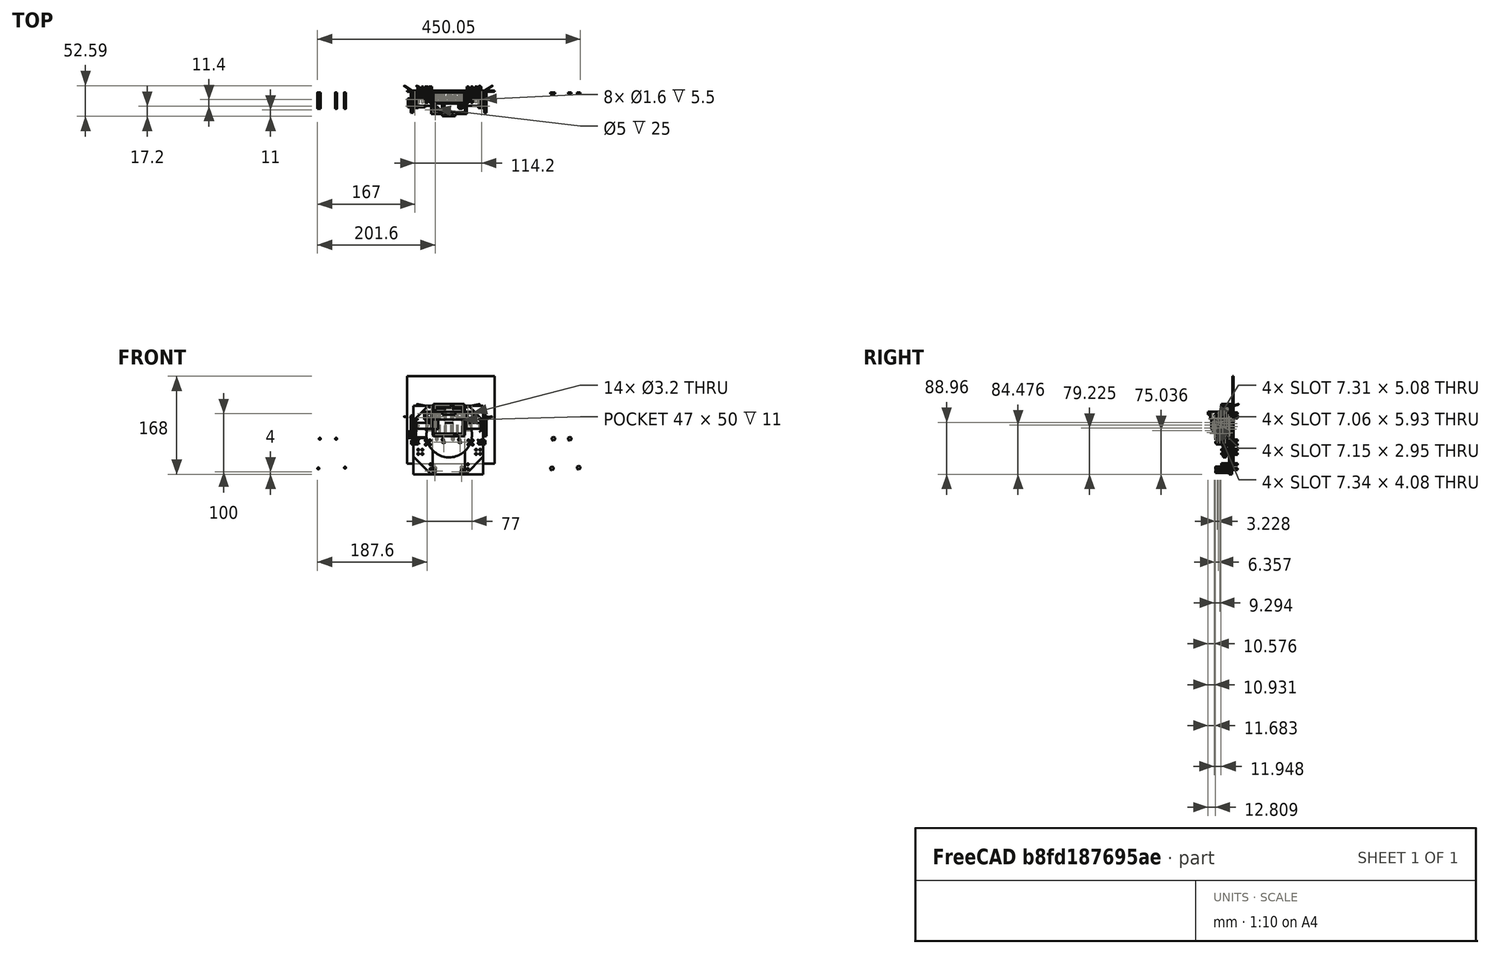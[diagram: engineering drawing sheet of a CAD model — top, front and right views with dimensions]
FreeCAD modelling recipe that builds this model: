
FCSTD DOCUMENT  (FreeCAD 0.16R6712 (Git))
Label: 5028.5 Blank Frank
License: All rights reserved
LicenseURL: http://en.wikipedia.org/wiki/All_rights_reserved
objects: Part::Cylinder×127, Part::Box×74, Part::Fuse×65, Part::Cut×64, Part::Feature×37, Part::MultiFuse×31, Part::Mirroring×14, Part::Chamfer×10, Part::Fillet×10, Part::Cone×8, Part::Compound×3, Part::Torus×2, App::DocumentObjectGroup×1
note: 445 computed .brp shape members not serialized (recipe doc carries the construction recipe); baked Part::Feature solids carry a one-line shape summary decoded from their .brp

FEATURE [Part::Cylinder] Cylinder
  Angle = 360
  Height = 30
  Radius = 7
FEATURE [Part::Cylinder] Cylinder001
  Angle = 360
  Height = 19
  Placement = pos=(0,0,30) rot=(0,0,1;0rad)
  Radius = 7
FEATURE [Part::Cylinder] Cylinder002
  Angle = 360
  Height = 1.8
  Placement = pos=(0,0,49) rot=(0,0,1;0rad)
  Radius = 2.5
FEATURE [Part::Compound] Compound
  Links = -> [Cylinder,Cylinder002,Cylinder001]
FEATURE [Part::Cylinder] Cylinder003
  Angle = 360
  Height = 30
  Radius = 7
FEATURE [Part::Cylinder] Cylinder004
  Angle = 360
  Height = 19
  Placement = pos=(0,0,30) rot=(0,0,1;0rad)
  Radius = 7
FEATURE [Part::Cylinder] Cylinder005
  Angle = 360
  Height = 1.8
  Placement = pos=(0,0,49) rot=(0,0,1;0rad)
  Radius = 2.5
FEATURE [Part::Compound] Compound001
  Links = -> [Cylinder003,Cylinder005,Cylinder004]
  Placement = pos=(14.5,0,50) rot=(1,0,0;3.14159rad)
FEATURE [Part::Cylinder] Cylinder006
  Angle = 360
  Height = 30
  Radius = 7
FEATURE [Part::Cylinder] Cylinder007
  Angle = 360
  Height = 19
  Placement = pos=(0,0,30) rot=(0,0,1;0rad)
  Radius = 7
FEATURE [Part::Cylinder] Cylinder008
  Angle = 360
  Height = 1.8
  Placement = pos=(0,0,49) rot=(0,0,1;0rad)
  Radius = 2.5
FEATURE [Part::Compound] Compound002
  Links = -> [Cylinder006,Cylinder008,Cylinder007]
  Placement = pos=(29,0,0) rot=(0,0,1;0rad)
FEATURE [Part::Box] Box  label="Cube"
  Height = 50
  Length = 47
  Placement = pos=(-9,-8,0) rot=(0,0,1;0rad)
  Width = 12
FEATURE [Part::Box] Box001  label="Cube001"
  Height = 55
  Length = 53
  Placement = pos=(-12,-8,-2.5) rot=(0,0,1;0rad)
  Width = 11
FEATURE [Part::Cylinder] Cylinder009
  Angle = 360
  Height = 50
  Radius = 7
FEATURE [Part::Cylinder] Cylinder010
  Angle = 360
  Height = 50
  Placement = pos=(14.5,0,0) rot=(0,0,1;0rad)
  Radius = 7
FEATURE [Part::Cut] Cut
  Base = -> Box001
  Tool = -> Box
FEATURE [Part::Box] Box002  label="Cube002"
  Height = 55
  Length = 53
  Placement = pos=(-12,3,-2.5) rot=(0,0,1;0rad)
  Width = 7
FEATURE [Part::Fuse] Fusion
  Base = -> Cut
  Tool = -> Box002
FEATURE [Part::Cut] Cut001  label="No idea why this is here...."
  Base = -> Fusion
  Tool = -> Cylinder009
FEATURE [Part::Cylinder] Cylinder011
  Angle = 360
  Height = 50
  Placement = pos=(29,0,0) rot=(0,0,1;0rad)
  Radius = 7
FEATURE [Part::Box] Box003  label="Cube003"
  Height = 5
  Length = 2
  Placement = pos=(28,-9,-2) rot=(0,0,1;0rad)
  Width = 12
FEATURE [Part::Box] Box004  label="Cube004"
  Height = 5
  Length = 2
  Placement = pos=(18.5,-9,46) rot=(0,0,1;0rad)
  Width = 12
FEATURE [Part::Box] Box005  label="Cube005"
  Height = 5
  Length = 2
  Placement = pos=(-2,-9,46) rot=(0,0,1;0rad)
  Width = 12
FEATURE [Part::Box] Box006  label="Cube006"
  Height = 5
  Length = 3
  Placement = pos=(35,-9,-4) rot=(0,0,1;0rad)
  Width = 12
FEATURE [Part::Cut] Cut008
FEATURE [Part::Torus] Torus001
  Angle1 = -180
  Angle2 = 180
  Angle3 = 360
  Placement = pos=(0,0,2) rot=(0,0,1;0rad)
  Radius1 = 19
  Radius2 = 1.5
FEATURE [Part::Cut] Cut009  label="wheel2"
  Base = -> Cut008
  Placement = pos=(75,-7,15) rot=(0,1,0;1.5708rad)
  Tool = -> Torus001
FEATURE [Part::Torus] Torus
  Angle1 = -180
  Angle2 = 180
  Angle3 = 360
  Placement = pos=(0,0,2) rot=(0,0,1;0rad)
  Radius1 = 19
  Radius2 = 1.5
FEATURE [Part::Cut] Cut010
FEATURE [Part::Cut] Cut011  label="wheel1"
  Base = -> Cut010
  Placement = pos=(-51,-7,15) rot=(0,1,0;1.5708rad)
  Tool = -> Torus
FEATURE [Part::Fuse] Fusion003
FEATURE [Part::Cylinder] Cylinder012
  Angle = 360
  Height = 10
  Placement = pos=(5,-4.5,0) rot=(0,1,0;1.5708rad)
  Radius = 0.8
FEATURE [Part::Fuse] Fusion048  label="right-motor001"
  Base = -> Cylinder012
  Placement = pos=(-51,-7,15) rot=(0,0,1;0rad)
  Tool = -> Fusion003
FEATURE [Part::Fuse] Fusion049
FEATURE [Part::Cylinder] Cylinder013
  Angle = 360
  Height = 10
  Placement = pos=(5,-4.5,0) rot=(0,1,0;1.5708rad)
  Radius = 0.8
FEATURE [Part::Fuse] Fusion050  label="left-motor001"
  Base = -> Cylinder013
  Placement = pos=(79,-7,15) rot=(0,0,1;3.14159rad)
  Tool = -> Fusion049
FEATURE [Part::Box] Box007  label="Cube007"
  Height = 5
  Length = 2
  Placement = pos=(37.5,-9,46) rot=(0,0,1;0rad)
  Width = 12
FEATURE [Part::Box] Box008  label="Cube008"
  Height = 5
  Length = 2
  Placement = pos=(8,-9,-2) rot=(0,0,1;0rad)
  Width = 12
FEATURE [Part::Box] Box009  label="The Ground"
  Height = 150
  Length = 150
  Placement = pos=(-57,11,-50) rot=(0,0,1;0rad)
  Width = 2
FEATURE [Part::Box] Box010  label="Motor Mount Left"
  Height = 16
  Length = 4
  Placement = pos=(69,-13,7) rot=(0,0,1;0rad)
  Width = 20
FEATURE [Part::Box] Box011  label="Motor Mount Right"
  Height = 16
  Length = 4
  Placement = pos=(-46,-13,7) rot=(0,0,1;0rad)
  Width = 20
FEATURE [Part::Box] Box012  label="Motor Support Right"
  Height = 16
  Length = 10
  Placement = pos=(-25,-1,7) rot=(0,0,1;0rad)
  Width = 8
FEATURE [Part::Box] Box013  label="Motor Support Left"
  Height = 16
  Length = 10
  Placement = pos=(43,-1,7) rot=(0,0,1;0rad)
  Width = 8
FEATURE [Part::Cylinder] Cylinder014
  Angle = 360
  Height = 28
  Placement = pos=(40.7,0,-10.3) rot=(1,0,0;1.5708rad)
  Radius = 1.6
FEATURE [Part::Cylinder] Cylinder015
  Angle = 360
  Height = 28
  Placement = pos=(-2.4,0,-59.8) rot=(1,0,0;1.5708rad)
  Radius = 1.6
FEATURE [Part::Cylinder] Cylinder016
  Angle = 360
  Height = 28
  Placement = pos=(-5,0,-9) rot=(1,0,0;1.5708rad)
  Radius = 1.6
FEATURE [Part::Cylinder] Cylinder017
  Angle = 360
  Height = 28
  Placement = pos=(25.5,0,-59.8) rot=(1,0,0;1.5708rad)
  Radius = 1.6
FEATURE [Part::Fuse] Fusion051
  Base = -> Cylinder015
  Tool = -> Cylinder016
FEATURE [Part::Fuse] Fusion052
  Base = -> Cylinder014
  Tool = -> Cylinder017
FEATURE [Part::Fuse] Fusion053  label="Screw holes on Arduino Duo"
  Base = -> Fusion051
  Tool = -> Fusion052
FEATURE [Part::Mirroring] Part__Mirroring  label="XXXXXScrew holes on Arduino Duo (Mirror #1)"
  Base = (0,0,0)
  Normal = (0,0,1)
  Placement = pos=(-204,10,-67) rot=(0,0,1;0rad)
  Source = -> Fusion053
FEATURE [Part::Box] Box014  label="Not used Cube"
  Height = 10
  Length = 10
  Placement = pos=(-1,4,-5.85) rot=(0,0,1;0rad)
  Width = 10
FEATURE [Part::Box] Box015  label="Cube014 Arduino Support cube"
  Height = 67
  Length = 55
  Placement = pos=(-13,5,-68) rot=(0,0,1;0rad)
  Width = 5
FEATURE [Part::Cylinder] Cylinder018
  Angle = 360
  Height = 5
  Placement = pos=(15,0,0) rot=(1,0,0;1.5708rad)
  Radius = 39
FEATURE [Part::Cut] Cut014  label="M3 Nut"
  Base = -> Cut001
  Placement = pos=(-6.4,10,-7.2) rot=(1,0,0;1.5708rad)
  Tool = -> Cylinder001
FEATURE [Part::Cut] Cut015  label="M3 Nut001"
  Base = -> Cut001
  Placement = pos=(21.5,10,-7.2) rot=(1,0,0;1.5708rad)
  Tool = -> Cylinder001
FEATURE [Part::Cut] Cut016  label="M3 Nut002"
  Base = -> Cut001
  Placement = pos=(36.7,10,-56.7) rot=(1,0,0;1.5708rad)
  Tool = -> Cylinder001
FEATURE [Part::Cut] Cut017  label="M3 Nut003"
  Base = -> Cut001
  Placement = pos=(-9,10,-58) rot=(1,0,0;1.5708rad)
  Tool = -> Cylinder001
FEATURE [Part::Cut] Cut018
  Base = -> Cut
  Placement = pos=(-9,10,-58) rot=(1,0,0;1.5708rad)
  Tool = -> Box006
FEATURE [Part::Cut] Cut019
  Base = -> Cut
  Placement = pos=(36.7,10,-56.7) rot=(1,0,0;1.5708rad)
  Tool = -> Box006
FEATURE [Part::Cut] Cut020
  Base = -> Cut
  Placement = pos=(-6.4,10,-7.2) rot=(1,0,0;1.5708rad)
  Tool = -> Box006
FEATURE [Part::Cut] Cut021
  Base = -> Cut
  Placement = pos=(21.5,10,-7.2) rot=(1,0,0;1.5708rad)
  Tool = -> Box006
FEATURE [Part::MultiFuse] Fusion054  label="XXXXXHex Holes"
  Placement = pos=(200,0,0) rot=(0,0,1;0rad)
  Shapes = -> [Cut018,Cut021,Cut019,Cut020]
FEATURE [Part::Box] Box016  label="Cube015"
  Height = 117
  Length = 33
  Placement = pos=(-46,7,-68) rot=(0,0,1;0rad)
  Width = 3
FEATURE [Part::Box] Box017  label="Cube016"
  Height = 117
  Length = 31
  Placement = pos=(42,7,-68) rot=(0,0,1;0rad)
  Width = 3
FEATURE [Part::Cylinder] Cylinder019
  Angle = 360
  Height = 28
  Placement = pos=(48,20,-10) rot=(1,0,0;1.5708rad)
  Radius = 1.6
FEATURE [Part::Cylinder] Cylinder020
  Angle = 360
  Height = 28
  Placement = pos=(47,20,-51) rot=(1,0,0;1.5708rad)
  Radius = 1.6
FEATURE [Part::Cylinder] Cylinder021
  Angle = 360
  Height = 28
  Placement = pos=(48,20,-17) rot=(1,0,0;1.5708rad)
  Radius = 1.6
FEATURE [Part::Cylinder] Cylinder022
  Angle = 360
  Height = 28
  Placement = pos=(47,20,-59) rot=(1,0,0;1.5708rad)
  Radius = 1.6
FEATURE [Part::Cylinder] Cylinder023
  Angle = 360
  Height = 28
  Placement = pos=(55,20,-17) rot=(1,0,0;1.5708rad)
  Radius = 1.6
FEATURE [Part::Cylinder] Cylinder024
  Angle = 360
  Height = 28
  Placement = pos=(55,20,-10) rot=(1,0,0;1.5708rad)
  Radius = 1.6
FEATURE [Part::MultiFuse] Fusion055
  Shapes = -> [Cylinder021,Cylinder023,Cylinder024,Cylinder019]
FEATURE [Part::MultiFuse] Fusion056
  Placement = pos=(13,0,-16) rot=(0,0,1;0rad)
  Shapes = -> [Cylinder021,Cylinder023,Cylinder024,Cylinder019]
FEATURE [Part::MultiFuse] Fusion057  label="Mount holes top left"
  Placement = pos=(-1,0,46) rot=(0,0,1;0rad)
  Shapes = -> [Cylinder021,Cylinder023,Cylinder024,Cylinder019]
FEATURE [Part::MultiFuse] Fusion058  label="Mount holes top right"
  Placement = pos=(-71,0,46) rot=(0,0,1;0rad)
  Shapes = -> [Cylinder021,Cylinder023,Cylinder024,Cylinder019]
FEATURE [Part::MultiFuse] Fusion059
  Shapes = -> [Cylinder022,Cylinder020,Fusion055,Fusion056]
FEATURE [Part::Mirroring] Part__Mirroring001  label="Mount holes bottom right"
  Base = (0,0,0)
  Normal = (1,0,0)
  Placement = pos=(30,0,0) rot=(0,0,1;0rad)
  Source = -> Fusion059
FEATURE [Part::Cylinder] Cylinder025
  Angle = 360
  Height = 28
  Placement = pos=(48,20,-10) rot=(1,0,0;1.5708rad)
  Radius = 1.6
FEATURE [Part::Cylinder] Cylinder026
  Angle = 360
  Height = 28
  Placement = pos=(47,20,-51) rot=(1,0,0;1.5708rad)
  Radius = 1.6
FEATURE [Part::Cylinder] Cylinder027
  Angle = 360
  Height = 28
  Placement = pos=(48,20,-17) rot=(1,0,0;1.5708rad)
  Radius = 1.6
FEATURE [Part::Cylinder] Cylinder028
  Angle = 360
  Height = 28
  Placement = pos=(47,20,-59) rot=(1,0,0;1.5708rad)
  Radius = 1.6
FEATURE [Part::Cylinder] Cylinder029
  Angle = 360
  Height = 28
  Placement = pos=(55,20,-17) rot=(1,0,0;1.5708rad)
  Radius = 1.6
FEATURE [Part::Cylinder] Cylinder030
  Angle = 360
  Height = 28
  Placement = pos=(55,20,-10) rot=(1,0,0;1.5708rad)
  Radius = 1.6
FEATURE [Part::MultiFuse] Fusion060
  Shapes = -> [Cylinder027,Cylinder029,Cylinder030,Cylinder025]
FEATURE [Part::MultiFuse] Fusion061
  Placement = pos=(13,0,-16) rot=(0,0,1;0rad)
  Shapes = -> [Cylinder027,Cylinder029,Cylinder030,Cylinder025]
FEATURE [Part::MultiFuse] Fusion062  label="Mount holes bottom left"
  Shapes = -> [Cylinder028,Cylinder026,Fusion060,Fusion061]
FEATURE [Part::Cylinder] Cylinder031  label="Cylinder127"
  Angle = 360
  Height = 10
  Placement = pos=(0,18,29) rot=(0,0,1;0rad)
  Radius = 2.25
FEATURE [Part::Cylinder] Cylinder032  label="Cylinder128"
  Angle = 360
  Height = 10
  Placement = pos=(4.5,18,32) rot=(0,0,1;0rad)
  Radius = 1
FEATURE [Part::Cylinder] Cylinder033  label="Cylinder129"
  Angle = 360
  Height = 10
  Placement = pos=(-4.5,18,32) rot=(0,0,1;0rad)
  Radius = 1
FEATURE [Part::Fuse] Fusion009  label="Mounting Screw Holes"
  Base = -> Cylinder032
  Tool = -> Cylinder033
FEATURE [Part::Fuse] Fusion071  label="Motor Holes Left"
  Base = -> Cylinder031
  Placement = pos=(37,-7,-3) rot=(0.57735,0.57735,0.57735;2.0944rad)
  Tool = -> Fusion009
FEATURE [Part::Cylinder] Cylinder034  label="Cylinder130"
  Angle = 360
  Height = 10
  Placement = pos=(0,18,29) rot=(0,0,1;0rad)
  Radius = 2.25
FEATURE [Part::Cylinder] Cylinder035  label="Cylinder131"
  Angle = 360
  Height = 10
  Placement = pos=(4.5,18,32) rot=(0,0,1;0rad)
  Radius = 1
FEATURE [Part::Cylinder] Cylinder036  label="Cylinder132"
  Angle = 360
  Height = 10
  Placement = pos=(-4.5,18,32) rot=(0,0,1;0rad)
  Radius = 1
FEATURE [Part::Fuse] Fusion072  label="Mounting Screw Holes001"
  Base = -> Cylinder035
  Tool = -> Cylinder036
FEATURE [Part::Fuse] Fusion073  label="Motor Holes Right"
  Base = -> Cylinder034
  Placement = pos=(-79,-7,-3) rot=(0.57735,0.57735,0.57735;2.0944rad)
  Tool = -> Fusion072
FEATURE [Part::Cylinder] Cylinder037  label="Cylinder133"
  Angle = 360
  Height = 28
  Placement = pos=(40.7,0,-10.3) rot=(1,0,0;1.5708rad)
  Radius = 1.6
FEATURE [Part::Cylinder] Cylinder038  label="Cylinder134"
  Angle = 360
  Height = 28
  Placement = pos=(-2.4,0,-59.8) rot=(1,0,0;1.5708rad)
  Radius = 1.6
FEATURE [Part::Cylinder] Cylinder039  label="Cylinder135"
  Angle = 360
  Height = 28
  Placement = pos=(-5,0,-9) rot=(1,0,0;1.5708rad)
  Radius = 1.6
FEATURE [Part::Cylinder] Cylinder040  label="Cylinder136"
  Angle = 360
  Height = 28
  Placement = pos=(25.5,0,-59.8) rot=(1,0,0;1.5708rad)
  Radius = 1.6
FEATURE [Part::Fuse] Fusion074
  Base = -> Cylinder038
  Tool = -> Cylinder039
FEATURE [Part::Fuse] Fusion075
  Base = -> Cylinder037
  Tool = -> Cylinder040
FEATURE [Part::Fuse] Fusion076  label="Screw holes on Arduino Duo001"
  Base = -> Fusion074
  Tool = -> Fusion075
FEATURE [Part::Mirroring] Part__Mirroring002  label="Screw holes on Arduino Duo (Mirror #1)001"
  Base = (0,0,0)
  Normal = (0,0,1)
  Placement = pos=(-4,10,-67) rot=(0,0,1;0rad)
  Source = -> Fusion076
FEATURE [Part::Mirroring] Part__Mirroring003  label="Screw holes on Arduino Duo (Mirror #1)001 (Mirror #4)"
  Base = (0,0,0)
  Normal = (1,0,0)
  Placement = pos=(27,0,-6) rot=(0,0,1;0rad)
  Source = -> Part__Mirroring002
FEATURE [Part::Box] Box018  label="Cube017"
  Height = 50
  Length = 47
  Placement = pos=(-9,-8,0) rot=(0,0,1;0rad)
  Width = 12
FEATURE [Part::Box] Box019  label="Cube018"
  Height = 55
  Length = 53
  Placement = pos=(-12,-8,-2.5) rot=(0,0,1;0rad)
  Width = 11
FEATURE [Part::Cut] Cut031
  Base = -> Box019
  Tool = -> Box018
FEATURE [Part::Box] Box020  label="Cube019"
  Height = 5
  Length = 3
  Placement = pos=(35,-9,-4) rot=(0,0,1;0rad)
  Width = 12
FEATURE [Part::Cut] Cut032
  Base = -> Cut031
  Placement = pos=(-9,10,-58) rot=(1,0,0;1.5708rad)
  Tool = -> Box020
FEATURE [Part::Cut] Cut033
  Base = -> Cut031
  Placement = pos=(36.7,10,-56.7) rot=(1,0,0;1.5708rad)
  Tool = -> Box020
FEATURE [Part::Cut] Cut034
  Base = -> Cut031
  Placement = pos=(-6.4,10,-7.2) rot=(1,0,0;1.5708rad)
  Tool = -> Box020
FEATURE [Part::Cut] Cut035
  Base = -> Cut031
  Placement = pos=(21.5,10,-7.2) rot=(1,0,0;1.5708rad)
  Tool = -> Box020
FEATURE [Part::MultiFuse] Fusion077
  Shapes = -> [Cut032,Cut035,Cut033,Cut034]
FEATURE [Part::Mirroring] Part__Mirroring004  label="Hex Holes"
  Base = (0,0,0)
  Normal = (1,0,0)
  Placement = pos=(27,0,-6) rot=(0,0,1;0rad)
  Source = -> Fusion077
FEATURE [Part::Box] Box021  label="Cube020"
  Height = 13
  Length = 61
  Placement = pos=(-16,-27,26) rot=(0,0,1;0rad)
  Width = 34
FEATURE [Part::Box] Box022  label="Cube021"
  Height = 13
  Length = 12
  Placement = pos=(45,4,26) rot=(0,0,1;0rad)
  Width = 3
FEATURE [Part::Box] Box023  label="Cube022"
  Height = 13
  Length = 12
  Placement = pos=(-28,4,26) rot=(0,0,1;0rad)
  Width = 3
FEATURE [Part::Box] Box024  label="Cube023"
  Height = 13
  Length = 55
  Placement = pos=(-13,-24,26) rot=(0,0,1;0rad)
  Width = 31
FEATURE [Part::Cylinder] Cylinder041  label="Cylinder137"
  Angle = 360
  Height = 28
  Placement = pos=(54,20,29) rot=(1,0,0;1.5708rad)
  Radius = 1.6
FEATURE [Part::Cylinder] Cylinder042  label="Cylinder138"
  Angle = 360
  Height = 28
  Placement = pos=(54,20,36) rot=(1,0,0;1.5708rad)
  Radius = 1.6
FEATURE [Part::Cylinder] Cylinder043  label="Cylinder139"
  Angle = 360
  Height = 28
  Placement = pos=(-23,20,29) rot=(1,0,0;1.5708rad)
  Radius = 1.6
FEATURE [Part::Cylinder] Cylinder044  label="Cylinder140"
  Angle = 360
  Height = 28
  Placement = pos=(-23,20,36) rot=(1,0,0;1.5708rad)
  Radius = 1.6
FEATURE [Part::Cylinder] Cylinder045  label="Cylinder141"
  Angle = 360
  Height = 10
  Placement = pos=(36,-17.25,32.5) rot=(0,1,0;1.5708rad)
  Radius = 2.5
FEATURE [Part::Cut] Cut037
  Base = -> Box021
  Tool = -> Box024
FEATURE [Part::Cut] Cut038
  Base = -> Cut037
  Tool = -> Cylinder045
FEATURE [Part::Box] Box025  label="Cube024"
  Height = 5
  Length = 22
  Placement = pos=(3.5,-31,34) rot=(0,0,1;0rad)
  Width = 4
FEATURE [Part::Cylinder] Cylinder046  label="Cylinder142"
  Angle = 360
  Height = 10
  Placement = pos=(20.75,-29,30) rot=(0,0,1;0rad)
  Radius = 0.85
FEATURE [Part::Cylinder] Cylinder047  label="Cylinder143"
  Angle = 360
  Height = 10
  Placement = pos=(8.25,-29,40) rot=(1,0,0;3.14159rad)
  Radius = 0.85
FEATURE [Part::Fuse] Fusion078
  Base = -> Cylinder046
  Tool = -> Cylinder047
FEATURE [Part::Cut] Cut039
  Base = -> Box025
  Tool = -> Fusion078
FEATURE [Part::Fuse] Fusion079
  Base = -> Cut038
  Tool = -> Cut039
FEATURE [Part::Fuse] Fusion080
  Base = -> Cylinder043
  Tool = -> Cylinder044
FEATURE [Part::Fuse] Fusion081
  Base = -> Cylinder041
  Tool = -> Cylinder042
FEATURE [Part::Fuse] Fusion082
  Base = -> Box023
  Tool = -> Fusion079
FEATURE [Part::Fuse] Fusion083
  Base = -> Box022
  Tool = -> Fusion082
FEATURE [Part::Cut] Cut040
  Base = -> Fusion083
  Tool = -> Fusion081
FEATURE [Part::Cut] Cut041  label="Switch Bracket"
  Base = -> Cut040
  Tool = -> Fusion080
FEATURE [Part::Cylinder] Cylinder048  label="Cylinder144"
  Angle = 360
  Height = 28
  Placement = pos=(-23,20,29) rot=(1,0,0;1.5708rad)
  Radius = 1.6
FEATURE [Part::Cylinder] Cylinder049  label="Cylinder145"
  Angle = 360
  Height = 28
  Placement = pos=(-23,20,36) rot=(1,0,0;1.5708rad)
  Radius = 1.6
FEATURE [Part::Fuse] Fusion084
  Base = -> Cylinder048
  Placement = pos=(1,0,0) rot=(0,0,1;0rad)
  Tool = -> Cylinder049
FEATURE [Part::Cylinder] Cylinder050  label="Cylinder146"
  Angle = 360
  Height = 28
  Placement = pos=(-23,20,29) rot=(1,0,0;1.5708rad)
  Radius = 1.6
FEATURE [Part::Cylinder] Cylinder051  label="Cylinder147"
  Angle = 360
  Height = 28
  Placement = pos=(-23,20,36) rot=(1,0,0;1.5708rad)
  Radius = 1.6
FEATURE [Part::Fuse] Fusion085
  Base = -> Cylinder050
  Placement = pos=(-1,0,0) rot=(0,0,1;0rad)
  Tool = -> Cylinder051
FEATURE [Part::Cut] Cut042
  Base = -> Cut041
  Tool = -> Fusion084
FEATURE [Part::Cut] Cut043  label="Switch Bracket001"
  Base = -> Cut042
  Tool = -> Fusion085
FEATURE [Part::Cylinder] Cylinder052  label="Cylinder148"
  Angle = 360
  Height = 42
  Radius = 4.8
FEATURE [Part::Cylinder] Cylinder053  label="Cylinder149"
  Angle = 360
  Height = 1.6
  Placement = pos=(0,0,42) rot=(0,0,1;0rad)
  Radius = 1.65
FEATURE [Part::Fuse] Fusion086
  Base = -> Cylinder052
  Placement = pos=(2,0,0) rot=(0,0,1;0rad)
  Tool = -> Cylinder053
FEATURE [Part::Cylinder] Cylinder054  label="Cylinder150"
  Angle = 360
  Height = 42
  Radius = 4.8
FEATURE [Part::Cylinder] Cylinder055  label="Cylinder151"
  Angle = 360
  Height = 1.6
  Placement = pos=(0,0,42) rot=(0,0,1;0rad)
  Radius = 1.65
FEATURE [Part::Fuse] Fusion087
  Base = -> Cylinder054
  Placement = pos=(12,0,0) rot=(0,0,1;0rad)
  Tool = -> Cylinder055
FEATURE [Part::Cylinder] Cylinder056  label="Cylinder152"
  Angle = 360
  Height = 42
  Radius = 4.8
FEATURE [Part::Cylinder] Cylinder057  label="Cylinder153"
  Angle = 360
  Height = 1.6
  Placement = pos=(0,0,42) rot=(0,0,1;0rad)
  Radius = 1.65
FEATURE [Part::Fuse] Fusion088
  Base = -> Cylinder056
  Placement = pos=(22,0,0) rot=(0,0,1;0rad)
  Tool = -> Cylinder057
FEATURE [Part::Cylinder] Cylinder058  label="Cylinder154"
  Angle = 360
  Height = 42
  Radius = 4.8
FEATURE [Part::Cylinder] Cylinder059  label="Cylinder155"
  Angle = 360
  Height = 1.6
  Placement = pos=(0,0,42) rot=(0,0,1;0rad)
  Radius = 1.65
FEATURE [Part::Fuse] Fusion089
  Base = -> Cylinder058
  Placement = pos=(32,0,0) rot=(0,0,1;0rad)
  Tool = -> Cylinder059
FEATURE [Part::Cylinder] Cylinder060  label="Cylinder156"
  Angle = 360
  Height = 42
  Radius = 4.8
FEATURE [Part::Cylinder] Cylinder061  label="Cylinder157"
  Angle = 360
  Height = 1.6
  Placement = pos=(0,0,42) rot=(0,0,1;0rad)
  Radius = 1.65
FEATURE [Part::Fuse] Fusion093
  Base = -> Cylinder060
  Placement = pos=(-8,0,0) rot=(0,0,1;0rad)
  Tool = -> Cylinder061
FEATURE [Part::MultiFuse] Fusion094  label="AAA Batts"
  Placement = pos=(2.5,0,2) rot=(0,0,1;0rad)
  Shapes = -> [Fusion093,Fusion086,Fusion087,Fusion088,Fusion089]
FEATURE [Part::Cylinder] Cylinder062  label="Cylinder158"
  Angle = 360
  Height = 10
  Radius = 17
FEATURE [Part::Cylinder] Cylinder063  label="Cylinder159"
  Angle = 360
  Height = 16
  Placement = pos=(0,0,-4) rot=(0,0,1;0rad)
  Radius = 10
FEATURE [Part::Cut] Cut044
  Base = -> Cylinder062
  Tool = -> Cylinder063
FEATURE [Part::Box] Box026  label="Cube025"
  Height = 20
  Length = 18
  Placement = pos=(0,0,-5) rot=(0,0,1;0rad)
  Width = 20
FEATURE [Part::Box] Box027  label="Cube026"
  Height = 20
  Length = 10
  Placement = pos=(0,0,-5) rot=(0,0,1;0.174533rad)
  Width = 20
FEATURE [Part::Cut] Cut045
  Base = -> Box027
  Tool = -> Box026
FEATURE [Part::Feature] Cut045001
  Placement = pos=(0,0,0) rot=(0,0,1;0.349066rad)
  shape: bbox 10 x 22.32 x 20 mm, 7 faces (baked)
FEATURE [Part::Feature] Cut045002
  Placement = pos=(0,0,0) rot=(0,0,1;0.698132rad)
  shape: bbox 15.32 x 20.52 x 20 mm, 7 faces (baked)
FEATURE [Part::Feature] Cut045003
  Placement = pos=(0,0,0) rot=(0,0,1;1.0472rad)
  shape: bbox 18.79 x 16.24 x 20 mm, 7 faces (baked)
FEATURE [Part::Feature] Cut045004
  Placement = pos=(0,0,0) rot=(0,0,1;1.39626rad)
  shape: bbox 20 x 10 x 20 mm, 7 faces (baked)
FEATURE [Part::Feature] Cut045005
  Placement = pos=(0,0,0) rot=(0,0,1;1.74533rad)
  shape: bbox 22.21 x 9.894 x 20 mm, 7 faces (baked)
FEATURE [Part::Feature] Cut045006
  Placement = pos=(0,0,0) rot=(0,0,1;2.0944rad)
  shape: bbox 21.75 x 12.86 x 20 mm, 7 faces (baked)
FEATURE [Part::Feature] Cut045007
  Placement = pos=(0,0,0) rot=(0,0,1;2.44346rad)
  shape: bbox 18.66 x 17.32 x 20 mm, 7 faces (baked)
FEATURE [Part::Feature] Cut045008
  Placement = pos=(0,0,0) rot=(0,0,1;2.79253rad)
  shape: bbox 13.32 x 19.7 x 20 mm, 7 faces (baked)
FEATURE [Part::Feature] Cut045009
  Placement = pos=(0,0,0) rot=(0,0,1;3.14159rad)
  shape: bbox 10.1 x 21.43 x 20 mm, 7 faces (baked)
FEATURE [Part::Feature] Cut045010
  Placement = pos=(0,0,0) rot=(0,0,1;3.49066rad)
  shape: bbox 10 x 22.32 x 20 mm, 7 faces (baked)
FEATURE [Part::Feature] Cut045011
  Placement = pos=(0,0,0) rot=(0,0,1;3.83972rad)
  shape: bbox 15.32 x 20.52 x 20 mm, 7 faces (baked)
FEATURE [Part::Feature] Cut045012
  Placement = pos=(0,0,0) rot=(0,0,1;4.18879rad)
  shape: bbox 18.79 x 16.24 x 20 mm, 7 faces (baked)
FEATURE [Part::Feature] Cut045013
  Placement = pos=(0,0,0) rot=(0,0,-1;1.74533rad)
  shape: bbox 20 x 10 x 20 mm, 7 faces (baked)
FEATURE [Part::Feature] Cut045014
  Placement = pos=(0,0,0) rot=(0,0,-1;1.39626rad)
  shape: bbox 22.21 x 9.894 x 20 mm, 7 faces (baked)
FEATURE [Part::Feature] Cut045015
  Placement = pos=(0,0,0) rot=(0,0,-1;1.0472rad)
  shape: bbox 21.75 x 12.86 x 20 mm, 7 faces (baked)
FEATURE [Part::Feature] Cut045016
  Placement = pos=(0,0,0) rot=(0,0,-1;0.698132rad)
  shape: bbox 18.66 x 17.32 x 20 mm, 7 faces (baked)
FEATURE [Part::Feature] Cut045017
  Placement = pos=(0,0,0) rot=(0,0,-1;0.349066rad)
  shape: bbox 13.32 x 19.7 x 20 mm, 7 faces (baked)
FEATURE [Part::MultiFuse] Fusion095
  Shapes = -> [Cut045001,Cut045008,Cut045010,Cut045009,Cut045005,Cut045003,Cut045006,Cut045002,Cut045004,Cut045007,Cut045016,Cut045017,Cut045011,Cut045012,Cut045013,Cut045014,Cut045015,Cut045]
FEATURE [Part::Cut] Cut045018
  Base = -> Cut044
  Placement = pos=(72,-7,15) rot=(0,1,0;1.5708rad)
  Tool = -> Fusion095
FEATURE [Part::Cut] Cut045019  label="Wheel with Spokes AB"
  Base = -> Cut009
  Tool = -> Cut045018
FEATURE [Part::Box] Box028  label="Cube027"
  Height = 5
  Length = 2
  Placement = pos=(37.5,-9,-2) rot=(0,0,1;0rad)
  Width = 12
FEATURE [Part::Box] Box029  label="Cube028"
  Height = 50
  Length = 47
  Placement = pos=(-9,-8,0) rot=(0,0,1;0rad)
  Width = 12
FEATURE [Part::Box] Box030  label="Cube029"
  Height = 55
  Length = 53
  Placement = pos=(-12,-8,-2.5) rot=(0,0,1;0rad)
  Width = 11
FEATURE [Part::Cylinder] Cylinder064  label="Cylinder160"
  Angle = 360
  Height = 50
  Radius = 7
FEATURE [Part::Cut] Cut045020
  Base = -> Box030
  Tool = -> Box029
FEATURE [Part::Box] Box031  label="Cube030"
  Height = 55
  Length = 53
  Placement = pos=(-12,3,-2.5) rot=(0,0,1;0rad)
  Width = 7
FEATURE [Part::Fuse] Fusion096
  Base = -> Cut045020
  Tool = -> Box031
FEATURE [App::DocumentObjectGroup] Group  label="Older version parts"
  Group = -> [Compound,Compound001,Compound002,Cylinder064,Cylinder010,Cylinder011,Fusion096,Part__Mirroring,Fusion054,Part__Mirroring004,Cut014,Cut015,Cut016,Cut017]
FEATURE [Part::Box] Box032  label="Battery Base"
  Height = 50
  Length = 55
  Placement = pos=(-13,3,-1) rot=(0,0,1;0rad)
  Width = 7
FEATURE [Part::Box] Box033  label="Cube031"
  Height = 30
  Length = 10
  Placement = pos=(-14,-25,9) rot=(0,0,1;0rad)
  Width = 10
FEATURE [Part::Cylinder] Cylinder065  label="Cylinder161"
  Angle = 360
  Height = 43.5
  Placement = pos=(4,0,2) rot=(0,0,1;0rad)
  Radius = 4.8
FEATURE [Part::Cylinder] Cylinder066  label="Cylinder162"
  Angle = 360
  Height = 1.6
  Placement = pos=(4,0,44) rot=(0,0,1;0rad)
  Radius = 1.65
FEATURE [Part::Fuse] Fusion097
  Base = -> Cylinder065
  Tool = -> Cylinder066
FEATURE [Part::Cylinder] Cylinder067  label="Cylinder163"
  Angle = 360
  Height = 43.5
  Placement = pos=(14,0,2) rot=(0,0,1;0rad)
  Radius = 4.8
FEATURE [Part::Cylinder] Cylinder068  label="Cylinder164"
  Angle = 360
  Height = 1.6
  Placement = pos=(14,0,44) rot=(0,0,1;0rad)
  Radius = 1.65
FEATURE [Part::Fuse] Fusion098
  Base = -> Cylinder067
  Tool = -> Cylinder068
FEATURE [Part::Cylinder] Cylinder069  label="Cylinder165"
  Angle = 360
  Height = 43.5
  Placement = pos=(24,0,2) rot=(0,0,1;0rad)
  Radius = 4.8
FEATURE [Part::Cylinder] Cylinder070  label="Cylinder166"
  Angle = 360
  Height = 1.6
  Placement = pos=(24,0,44) rot=(0,0,1;0rad)
  Radius = 1.65
FEATURE [Part::Fuse] Fusion099
  Base = -> Cylinder069
  Tool = -> Cylinder070
FEATURE [Part::Cylinder] Cylinder071  label="Cylinder167"
  Angle = 360
  Height = 43.5
  Placement = pos=(34,0,2) rot=(0,0,1;0rad)
  Radius = 4.8
FEATURE [Part::Cylinder] Cylinder072  label="Cylinder168"
  Angle = 360
  Height = 1.6
  Placement = pos=(34,0,44) rot=(0,0,1;0rad)
  Radius = 1.65
FEATURE [Part::Fuse] Fusion100
  Base = -> Cylinder071
  Tool = -> Cylinder072
FEATURE [Part::Cylinder] Cylinder073  label="Cylinder169"
  Angle = 360
  Height = 43.5
  Placement = pos=(-6,0,2) rot=(0,0,1;0rad)
  Radius = 4.8
FEATURE [Part::Cylinder] Cylinder074  label="Cylinder170"
  Angle = 360
  Height = 1.6
  Placement = pos=(-6,0,44) rot=(0,0,1;0rad)
  Radius = 1.65
FEATURE [Part::Fuse] Fusion101
  Base = -> Cylinder073
  Tool = -> Cylinder074
FEATURE [Part::MultiFuse] Fusion102  label="AAA Batts001"
  Shapes = -> [Fusion101,Fusion097,Fusion098,Fusion099,Fusion100]
FEATURE [Part::Cylinder] Cylinder075  label="Cylinder171"
  Angle = 360
  Height = 10
  Placement = pos=(-9,-20,4) rot=(0,0,1;0rad)
  Radius = 2.75
FEATURE [Part::Cylinder] Cylinder076  label="Cylinder172"
  Angle = 360
  Height = 27
  Placement = pos=(-9,-20,14) rot=(0,0,1;0rad)
  Radius = 2.5
FEATURE [Part::Fuse] Fusion103  label="phototransistor hole"
  Base = -> Cylinder075
  Tool = -> Cylinder076
FEATURE [Part::Cut] Cut045021  label="Phototransistor holder"
  Base = -> Box033
  Tool = -> Fusion103
FEATURE [Part::Fuse] Fusion104  label="Switch Mount with phototransistor hole"
  Base = -> Cut043
  Tool = -> Cut045021
FEATURE [Part::Cut] Cut045022
  Base = -> Box032
  Tool = -> Fusion102
FEATURE [Part::Box] Box034  label="Cube032"
  Height = 2.5
  Length = 55
  Placement = pos=(-13,-9,-1) rot=(0,0,1;0rad)
  Width = 12
FEATURE [Part::Box] Box035  label="Cube033"
  Height = 2.5
  Length = 55
  Placement = pos=(-13,-9,46.5) rot=(0,0,1;0rad)
  Width = 12
FEATURE [Part::Box] Box036  label="Cube034"
  Height = 50
  Length = 2.5
  Placement = pos=(-13,-9,-1) rot=(0,0,1;0rad)
  Width = 12
FEATURE [Part::Box] Box037  label="Cube035"
  Height = 50
  Length = 2.5
  Placement = pos=(39.5,-9,-1) rot=(0,0,1;0rad)
  Width = 12
FEATURE [Part::MultiFuse] Fusion105
  Shapes = -> [Box034,Box036,Box037,Box035]
FEATURE [Part::Box] Box038  label="Cube036"
  Height = 5
  Length = 2
  Placement = pos=(-10.5,-9,46) rot=(0,0,1;0rad)
  Width = 12
FEATURE [Part::Box] Box039  label="Cube037"
  Height = 5
  Length = 2
  Placement = pos=(-10.5,-9,-2) rot=(0,0,1;0rad)
  Width = 12
FEATURE [Part::MultiFuse] Fusion106
  Shapes = -> [Box039,Box038,Box028,Box007]
FEATURE [Part::MultiFuse] Fusion107
  Shapes = -> [Box003,Box004,Box005,Box008]
FEATURE [Part::Cut] Cut045023
  Base = -> Fusion105
  Tool = -> Fusion106
FEATURE [Part::Cut] Cut045024
  Base = -> Cut045023
  Tool = -> Fusion107
FEATURE [Part::Box] Box040  label="Cube038"
  Height = 1.6
  Length = 30
  Placement = pos=(-56,-15.5,-6) rot=(0,0,1;0rad)
  Width = 15
FEATURE [Part::Box] Box041  label="Cube039"
  Height = 10
  Length = 14
  Placement = pos=(-56,-10.5,-4.5) rot=(0,0,1;0rad)
  Width = 6
FEATURE [Part::Box] Box042  label="Cube040"
  Height = 10
  Length = 5.3
  Placement = pos=(-51.7,-11.5,-4.5) rot=(0,0,1;0rad)
  Width = 8
FEATURE [Part::Cut] Cut045025
  Base = -> Box041
  Tool = -> Box042
FEATURE [Part::Fuse] Fusion108  label="Spoke Sensor PCB"
  Base = -> Box040
  Tool = -> Cut045025
FEATURE [Part::Cylinder] Cylinder077  label="Cylinder173"
  Angle = 360
  Height = 14.5
  Placement = pos=(-43.6,-2.4,-9) rot=(0,0,1;0rad)
  Radius = 0.8
FEATURE [Part::Cylinder] Cylinder078  label="Cylinder174"
  Angle = 360
  Height = 14.5
  Placement = pos=(-43.6,-13.8,-9) rot=(0,0,1;0rad)
  Radius = 0.8
FEATURE [Part::Fuse] Fusion109
  Base = -> Cylinder077
  Tool = -> Cylinder078
FEATURE [Part::Cut] Cut045026  label="Spoke Sensor PCB001"
  Base = -> Fusion108
  Tool = -> Fusion109
FEATURE [Part::Cylinder] Cylinder079  label="Cylinder175"
  Angle = 360
  Height = 14.5
  Placement = pos=(-43.6,-2.4,-18) rot=(0,0,1;0rad)
  Radius = 0.8
FEATURE [Part::Cylinder] Cylinder080  label="Cylinder176"
  Angle = 360
  Height = 14.5
  Placement = pos=(-43.6,-13.8,-18) rot=(0,0,1;0rad)
  Radius = 0.8
FEATURE [Part::Fuse] Fusion110  label="Batt Holder"
  Base = -> Cut045022
  Tool = -> Cut045024
FEATURE [Part::Box] Box043  label="Cube041"
  Height = 4
  Length = 12
  Placement = pos=(-50,-16.75,-17) rot=(0,0,1;0rad)
  Width = 26.75
FEATURE [Part::Chamfer] Chamfer
  Base = -> Box043
  Edges = 1 edges r=7: [Edge3]
FEATURE [Part::Cone] Cone
  Angle = 360
  Height = 1.5
  Placement = pos=(-43.6,-2.4,-13) rot=(0,0,1;0rad)
  Radius1 = 2.75
  Radius2 = 1.25
FEATURE [Part::Cone] Cone001
  Angle = 360
  Height = 1.5
  Placement = pos=(-43.6,-13.8,-13) rot=(0,0,1;0rad)
  Radius1 = 2.75
  Radius2 = 1.25
FEATURE [Part::Fuse] Fusion111
  Base = -> Cone
  Tool = -> Cone001
FEATURE [Part::Fuse] Fusion112
  Base = -> Chamfer
  Tool = -> Fusion111
FEATURE [Part::Fuse] Fusion113
  Base = -> Cylinder079
  Tool = -> Cylinder080
FEATURE [Part::Cut] Cut045027
  Base = -> Fusion112
  Tool = -> Fusion113
FEATURE [Part::Cylinder] Cylinder081  label="Cylinder177"
  Angle = 360
  Height = 14.5
  Placement = pos=(-43.6,-2.4,-18) rot=(0,0,1;0rad)
  Radius = 0.8
FEATURE [Part::Cylinder] Cylinder082  label="Cylinder178"
  Angle = 360
  Height = 14.5
  Placement = pos=(-43.6,-13.8,-18) rot=(0,0,1;0rad)
  Radius = 0.8
FEATURE [Part::Box] Box044  label="Cube042"
  Height = 4
  Length = 12
  Placement = pos=(-50,-16.75,-17) rot=(0,0,1;0rad)
  Width = 26.75
FEATURE [Part::Chamfer] Chamfer001
  Base = -> Box044
  Edges = 1 edges r=7: [Edge3]
FEATURE [Part::Cone] Cone002
  Angle = 360
  Height = 1.5
  Placement = pos=(-43.6,-2.4,-13) rot=(0,0,1;0rad)
  Radius1 = 2.75
  Radius2 = 1.25
FEATURE [Part::Cone] Cone003
  Angle = 360
  Height = 1.5
  Placement = pos=(-43.6,-13.8,-13) rot=(0,0,1;0rad)
  Radius1 = 2.75
  Radius2 = 1.25
FEATURE [Part::Fuse] Fusion114
  Base = -> Cone002
  Tool = -> Cone003
FEATURE [Part::Fuse] Fusion115
  Base = -> Chamfer001
  Tool = -> Fusion114
FEATURE [Part::Fuse] Fusion116
  Base = -> Cylinder081
  Tool = -> Cylinder082
FEATURE [Part::Cut] Cut045028
  Base = -> Fusion115
  Tool = -> Fusion116
FEATURE [Part::Mirroring] Part__Mirroring005  label="Cut045028 (Mirror #6)"
  Base = (0,0,0)
  Normal = (1,0,0)
  Placement = pos=(27,0,0) rot=(0,0,1;0rad)
  Source = -> Cut045028
FEATURE [Part::Box] Box045  label="Cube043"
  Height = 5
  Length = 2
  Placement = pos=(28,-9,-2) rot=(0,0,1;0rad)
  Width = 12
FEATURE [Part::Box] Box046  label="Cube044"
  Height = 5
  Length = 2
  Placement = pos=(18.5,-9,46) rot=(0,0,1;0rad)
  Width = 12
FEATURE [Part::Box] Box047  label="Cube045"
  Height = 5
  Length = 2
  Placement = pos=(-2,-9,46) rot=(0,0,1;0rad)
  Width = 12
FEATURE [Part::Box] Box048  label="Cube046"
  Height = 5
  Length = 2
  Placement = pos=(37.5,-9,46) rot=(0,0,1;0rad)
  Width = 12
FEATURE [Part::Box] Box049  label="Cube047"
  Height = 5
  Length = 2
  Placement = pos=(8,-9,-2) rot=(0,0,1;0rad)
  Width = 12
FEATURE [Part::Box] Box050  label="Motor Mount Left001"
  Height = 16
  Length = 4
  Placement = pos=(69,-13,7) rot=(0,0,1;0rad)
  Width = 20
FEATURE [Part::Box] Box051  label="Motor Mount Right001"
  Height = 16
  Length = 4
  Placement = pos=(-46,-13,7) rot=(0,0,1;0rad)
  Width = 20
FEATURE [Part::Box] Box052  label="Motor Support Right001"
  Height = 16
  Length = 10
  Placement = pos=(-25,-1,7) rot=(0,0,1;0rad)
  Width = 8
FEATURE [Part::Box] Box053  label="Motor Support Left001"
  Height = 16
  Length = 10
  Placement = pos=(43,-1,7) rot=(0,0,1;0rad)
  Width = 8
FEATURE [Part::Box] Box054  label="Cube014 Arduino Support cube001"
  Height = 67
  Length = 55
  Placement = pos=(-13,5,-68) rot=(0,0,1;0rad)
  Width = 5
FEATURE [Part::Box] Box055  label="Cube048"
  Height = 117
  Length = 33
  Placement = pos=(-46,7,-68) rot=(0,0,1;0rad)
  Width = 3
FEATURE [Part::Box] Box056  label="Cube049"
  Height = 117
  Length = 31
  Placement = pos=(42,7,-68) rot=(0,0,1;0rad)
  Width = 3
FEATURE [Part::Cylinder] Cylinder083  label="Cylinder179"
  Angle = 360
  Height = 28
  Placement = pos=(48,20,-10) rot=(1,0,0;1.5708rad)
  Radius = 1.6
FEATURE [Part::Cylinder] Cylinder084  label="Cylinder180"
  Angle = 360
  Height = 28
  Placement = pos=(48,20,-17) rot=(1,0,0;1.5708rad)
  Radius = 1.6
FEATURE [Part::Cylinder] Cylinder085  label="Cylinder181"
  Angle = 360
  Height = 28
  Placement = pos=(55,20,-17) rot=(1,0,0;1.5708rad)
  Radius = 1.6
FEATURE [Part::Cylinder] Cylinder086  label="Cylinder182"
  Angle = 360
  Height = 28
  Placement = pos=(55,20,-10) rot=(1,0,0;1.5708rad)
  Radius = 1.6
FEATURE [Part::MultiFuse] Fusion117  label="Mount holes top left001"
  Placement = pos=(-1,0,46) rot=(0,0,1;0rad)
  Shapes = -> [Cylinder084,Cylinder085,Cylinder086,Cylinder083]
FEATURE [Part::MultiFuse] Fusion118  label="Mount holes top right001"
  Placement = pos=(-71,0,46) rot=(0,0,1;0rad)
  Shapes = -> [Cylinder084,Cylinder085,Cylinder086,Cylinder083]
FEATURE [Part::Cylinder] Cylinder087  label="Cylinder183"
  Angle = 360
  Height = 10
  Placement = pos=(0,18,29) rot=(0,0,1;0rad)
  Radius = 2.25
FEATURE [Part::Cylinder] Cylinder088  label="Cylinder184"
  Angle = 360
  Height = 10
  Placement = pos=(4.5,18,32) rot=(0,0,1;0rad)
  Radius = 1
FEATURE [Part::Cylinder] Cylinder089  label="Cylinder185"
  Angle = 360
  Height = 10
  Placement = pos=(-4.5,18,32) rot=(0,0,1;0rad)
  Radius = 1
FEATURE [Part::Fuse] Fusion119  label="Mounting Screw Holes002"
  Base = -> Cylinder088
  Tool = -> Cylinder089
FEATURE [Part::Fuse] Fusion120  label="Motor Holes Left001"
  Base = -> Cylinder087
  Placement = pos=(37,-7,-3) rot=(0.57735,0.57735,0.57735;2.0944rad)
  Tool = -> Fusion119
FEATURE [Part::Cylinder] Cylinder090  label="Cylinder186"
  Angle = 360
  Height = 10
  Placement = pos=(0,18,29) rot=(0,0,1;0rad)
  Radius = 2.25
FEATURE [Part::Cylinder] Cylinder091  label="Cylinder187"
  Angle = 360
  Height = 10
  Placement = pos=(4.5,18,32) rot=(0,0,1;0rad)
  Radius = 1
FEATURE [Part::Cylinder] Cylinder092  label="Cylinder188"
  Angle = 360
  Height = 10
  Placement = pos=(-4.5,18,32) rot=(0,0,1;0rad)
  Radius = 1
FEATURE [Part::Fuse] Fusion121  label="Mounting Screw Holes003"
  Base = -> Cylinder091
  Tool = -> Cylinder092
FEATURE [Part::Fuse] Fusion122  label="Motor Holes Right001"
  Base = -> Cylinder090
  Placement = pos=(-79,-7,-3) rot=(0.57735,0.57735,0.57735;2.0944rad)
  Tool = -> Fusion121
FEATURE [Part::Cylinder] Cylinder093  label="Cylinder189"
  Angle = 360
  Height = 28
  Placement = pos=(40.7,0,-10.3) rot=(1,0,0;1.5708rad)
  Radius = 1.6
FEATURE [Part::Cylinder] Cylinder094  label="Cylinder190"
  Angle = 360
  Height = 28
  Placement = pos=(-2.4,0,-59.8) rot=(1,0,0;1.5708rad)
  Radius = 1.6
FEATURE [Part::Cylinder] Cylinder095  label="Cylinder191"
  Angle = 360
  Height = 28
  Placement = pos=(-5,0,-9) rot=(1,0,0;1.5708rad)
  Radius = 1.6
FEATURE [Part::Cylinder] Cylinder096  label="Cylinder192"
  Angle = 360
  Height = 28
  Placement = pos=(25.5,0,-59.8) rot=(1,0,0;1.5708rad)
  Radius = 1.6
FEATURE [Part::Fuse] Fusion123
  Base = -> Cylinder094
  Tool = -> Cylinder095
FEATURE [Part::Fuse] Fusion124
  Base = -> Cylinder093
  Tool = -> Cylinder096
FEATURE [Part::Fuse] Fusion125  label="Screw holes on Arduino Duo002"
  Base = -> Fusion123
  Tool = -> Fusion124
FEATURE [Part::Mirroring] Part__Mirroring006  label="Screw holes on Arduino Duo (Mirror #1)002"
  Base = (0,0,0)
  Normal = (0,0,1)
  Placement = pos=(-4,10,-67) rot=(0,0,1;0rad)
  Source = -> Fusion125
FEATURE [Part::Mirroring] Part__Mirroring007  label="Screw holes on Arduino Duo (Mirror #1)001 (Mirror #4)001"
  Base = (0,0,0)
  Normal = (1,0,0)
  Placement = pos=(27,0,-6) rot=(0,0,1;0rad)
  Source = -> Part__Mirroring006
FEATURE [Part::Box] Box057  label="Cube050"
  Height = 50
  Length = 47
  Placement = pos=(-9,-8,0) rot=(0,0,1;0rad)
  Width = 12
FEATURE [Part::Box] Box058  label="Cube051"
  Height = 55
  Length = 53
  Placement = pos=(-12,-8,-2.5) rot=(0,0,1;0rad)
  Width = 11
FEATURE [Part::Cut] Cut045029
  Base = -> Box058
  Tool = -> Box057
FEATURE [Part::Box] Box059  label="Cube052"
  Height = 5
  Length = 3
  Placement = pos=(35,-9,-4) rot=(0,0,1;0rad)
  Width = 12
FEATURE [Part::Cut] Cut045030
  Base = -> Cut045029
  Placement = pos=(-9,10,-58) rot=(1,0,0;1.5708rad)
  Tool = -> Box059
FEATURE [Part::Cut] Cut045031
  Base = -> Cut045029
  Placement = pos=(36.7,10,-56.7) rot=(1,0,0;1.5708rad)
  Tool = -> Box059
FEATURE [Part::Cut] Cut045032
  Base = -> Cut045029
  Placement = pos=(-6.4,10,-7.2) rot=(1,0,0;1.5708rad)
  Tool = -> Box059
FEATURE [Part::Cut] Cut045033
  Base = -> Cut045029
  Placement = pos=(21.5,10,-7.2) rot=(1,0,0;1.5708rad)
  Tool = -> Box059
FEATURE [Part::MultiFuse] Fusion126
  Shapes = -> [Cut045030,Cut045033,Cut045031,Cut045032]
FEATURE [Part::Mirroring] Part__Mirroring008  label="Hex Holes001"
  Base = (0,0,0)
  Normal = (1,0,0)
  Placement = pos=(27,0,-6) rot=(0,0,1;0rad)
  Source = -> Fusion126
FEATURE [Part::Box] Box060  label="Cube053"
  Height = 5
  Length = 2
  Placement = pos=(37.5,-9,-2) rot=(0,0,1;0rad)
  Width = 12
FEATURE [Part::Box] Box061  label="Battery Base001"
  Height = 50
  Length = 55
  Placement = pos=(-13,3,-1) rot=(0,0,1;0rad)
  Width = 7
FEATURE [Part::Cylinder] Cylinder097  label="Cylinder193"
  Angle = 360
  Height = 42
  Radius = 4.8
FEATURE [Part::Cylinder] Cylinder098  label="Cylinder194"
  Angle = 360
  Height = 1.6
  Placement = pos=(0,0,42) rot=(0,0,1;0rad)
  Radius = 1.65
FEATURE [Part::Fuse] Fusion127
  Base = -> Cylinder097
  Placement = pos=(2,0,0) rot=(0,0,1;0rad)
  Tool = -> Cylinder098
FEATURE [Part::Cylinder] Cylinder099  label="Cylinder195"
  Angle = 360
  Height = 42
  Radius = 4.8
FEATURE [Part::Cylinder] Cylinder100  label="Cylinder196"
  Angle = 360
  Height = 1.6
  Placement = pos=(0,0,42) rot=(0,0,1;0rad)
  Radius = 1.65
FEATURE [Part::Fuse] Fusion128
  Base = -> Cylinder099
  Placement = pos=(12,0,0) rot=(0,0,1;0rad)
  Tool = -> Cylinder100
FEATURE [Part::Cylinder] Cylinder101  label="Cylinder197"
  Angle = 360
  Height = 42
  Radius = 4.8
FEATURE [Part::Cylinder] Cylinder102  label="Cylinder198"
  Angle = 360
  Height = 1.6
  Placement = pos=(0,0,42) rot=(0,0,1;0rad)
  Radius = 1.65
FEATURE [Part::Fuse] Fusion129
  Base = -> Cylinder101
  Placement = pos=(22,0,0) rot=(0,0,1;0rad)
  Tool = -> Cylinder102
FEATURE [Part::Cylinder] Cylinder103  label="Cylinder199"
  Angle = 360
  Height = 42
  Radius = 4.8
FEATURE [Part::Cylinder] Cylinder104  label="Cylinder200"
  Angle = 360
  Height = 1.6
  Placement = pos=(0,0,42) rot=(0,0,1;0rad)
  Radius = 1.65
FEATURE [Part::Fuse] Fusion130
  Base = -> Cylinder103
  Placement = pos=(32,0,0) rot=(0,0,1;0rad)
  Tool = -> Cylinder104
FEATURE [Part::Cylinder] Cylinder105  label="Cylinder201"
  Angle = 360
  Height = 42
  Radius = 4.8
FEATURE [Part::Cylinder] Cylinder106  label="Cylinder202"
  Angle = 360
  Height = 1.6
  Placement = pos=(0,0,42) rot=(0,0,1;0rad)
  Radius = 1.65
FEATURE [Part::Fuse] Fusion131
  Base = -> Cylinder105
  Placement = pos=(-8,0,0) rot=(0,0,1;0rad)
  Tool = -> Cylinder106
FEATURE [Part::MultiFuse] Fusion132  label="AAA Batts002"
  Placement = pos=(2,0,2) rot=(0,0,1;0rad)
  Shapes = -> [Fusion131,Fusion127,Fusion128,Fusion129,Fusion130]
FEATURE [Part::Cut] Cut045034
  Base = -> Box061
  Tool = -> Fusion132
FEATURE [Part::Box] Box062  label="Cube054"
  Height = 2.5
  Length = 55
  Placement = pos=(-13,-9,-1) rot=(0,0,1;0rad)
  Width = 12
FEATURE [Part::Box] Box063  label="Cube055"
  Height = 2.5
  Length = 55
  Placement = pos=(-13,-9,46.5) rot=(0,0,1;0rad)
  Width = 12
FEATURE [Part::Box] Box064  label="Cube056"
  Height = 50
  Length = 2.5
  Placement = pos=(-13,-9,-1) rot=(0,0,1;0rad)
  Width = 12
FEATURE [Part::Box] Box065  label="Cube057"
  Height = 50
  Length = 2.5
  Placement = pos=(39.5,-9,-1) rot=(0,0,1;0rad)
  Width = 12
FEATURE [Part::MultiFuse] Fusion133
  Shapes = -> [Box062,Box064,Box065,Box063]
FEATURE [Part::Box] Box066  label="Cube058"
  Height = 5
  Length = 2
  Placement = pos=(-10.5,-9,46) rot=(0,0,1;0rad)
  Width = 12
FEATURE [Part::Box] Box067  label="Cube059"
  Height = 5
  Length = 2
  Placement = pos=(-10.5,-9,-2) rot=(0,0,1;0rad)
  Width = 12
FEATURE [Part::MultiFuse] Fusion134
  Shapes = -> [Box067,Box066,Box060,Box048]
FEATURE [Part::MultiFuse] Fusion135
  Shapes = -> [Box045,Box046,Box047,Box049]
FEATURE [Part::Cut] Cut045035
  Base = -> Fusion133
  Tool = -> Fusion134
FEATURE [Part::Cut] Cut045036
  Base = -> Cut045035
  Tool = -> Fusion135
FEATURE [Part::Cylinder] Cylinder107  label="Cylinder203"
  Angle = 360
  Height = 14.5
  Placement = pos=(-43.6,-2.4,-15) rot=(0,0,1;0rad)
  Radius = 0.8
FEATURE [Part::Cylinder] Cylinder108  label="Cylinder204"
  Angle = 360
  Height = 14.5
  Placement = pos=(-43.6,-13.8,-15) rot=(0,0,1;0rad)
  Radius = 0.8
FEATURE [Part::Fuse] Fusion136
  Base = -> Cut045034
  Tool = -> Cut045036
FEATURE [Part::Box] Box068  label="Cube060"
  Height = 4
  Length = 12
  Placement = pos=(-50,-16.75,-14) rot=(0,0,1;0rad)
  Width = 26.75
FEATURE [Part::Chamfer] Chamfer002
  Base = -> Box068
  Edges = 1 edges r=7: [Edge3]
FEATURE [Part::Cone] Cone004
  Angle = 360
  Height = 1.5
  Placement = pos=(-43.6,-2.4,-10) rot=(0,0,1;0rad)
  Radius1 = 2.75
  Radius2 = 1.25
FEATURE [Part::Cone] Cone005
  Angle = 360
  Height = 1.5
  Placement = pos=(-43.6,-13.8,-10) rot=(0,0,1;0rad)
  Radius1 = 2.75
  Radius2 = 1.25
FEATURE [Part::Fuse] Fusion137
  Base = -> Cone004
  Tool = -> Cone005
FEATURE [Part::Fuse] Fusion138
  Base = -> Chamfer002
  Tool = -> Fusion137
FEATURE [Part::Fuse] Fusion139
  Base = -> Cylinder107
  Tool = -> Cylinder108
FEATURE [Part::Cut] Cut045037
  Base = -> Fusion138
  Tool = -> Fusion139
FEATURE [Part::Cylinder] Cylinder109  label="Cylinder205"
  Angle = 360
  Height = 14.5
  Placement = pos=(-43.6,-2.4,-15) rot=(0,0,1;0rad)
  Radius = 0.8
FEATURE [Part::Cylinder] Cylinder110  label="Cylinder206"
  Angle = 360
  Height = 14.5
  Placement = pos=(-43.6,-13.8,-15) rot=(0,0,1;0rad)
  Radius = 0.8
FEATURE [Part::Box] Box069  label="Cube061"
  Height = 4
  Length = 12
  Placement = pos=(-50,-16.75,-14) rot=(0,0,1;0rad)
  Width = 26.75
FEATURE [Part::Chamfer] Chamfer003
  Base = -> Box069
  Edges = 1 edges r=7: [Edge3]
FEATURE [Part::Cone] Cone006
  Angle = 360
  Height = 1.5
  Placement = pos=(-43.6,-2.4,-10) rot=(0,0,1;0rad)
  Radius1 = 2.75
  Radius2 = 1.25
FEATURE [Part::Cone] Cone007
  Angle = 360
  Height = 1.5
  Placement = pos=(-43.6,-13.8,-10) rot=(0,0,1;0rad)
  Radius1 = 2.75
  Radius2 = 1.25
FEATURE [Part::Fuse] Fusion140
  Base = -> Cone006
  Tool = -> Cone007
FEATURE [Part::Fuse] Fusion141
  Base = -> Chamfer003
  Tool = -> Fusion140
FEATURE [Part::Fuse] Fusion142
  Base = -> Cylinder109
  Tool = -> Cylinder110
FEATURE [Part::Cut] Cut045038
  Base = -> Fusion141
  Tool = -> Fusion142
FEATURE [Part::Mirroring] Part__Mirroring009  label="Cut045028 (Mirror #6)001"
  Base = (0,0,0)
  Normal = (1,0,0)
  Placement = pos=(27,0,0) rot=(0,0,1;0rad)
  Source = -> Cut045038
FEATURE [Part::Cut] Cut045039
  Base = -> Box050
  Tool = -> Fusion120
FEATURE [Part::Cut] Cut045040
  Base = -> Box051
  Tool = -> Fusion122
FEATURE [Part::MultiFuse] Fusion143
  Shapes = -> [Box054,Box055,Box056]
FEATURE [Part::Fuse] Fusion144
  Base = -> Fusion136
  Tool = -> Fusion143
FEATURE [Part::MultiFuse] Fusion145
  Shapes = -> [Fusion144,Cut045040,Cut045039]
FEATURE [Part::MultiFuse] Fusion146
  Shapes = -> [Fusion145,Part__Mirroring009,Cut045037]
FEATURE [Part::Cut] Cut045041
  Base = -> Fusion146
  Tool = -> Fusion117
FEATURE [Part::Cut] Cut045042
  Base = -> Cut045041
  Tool = -> Fusion118
FEATURE [Part::Cut] Cut045043
  Base = -> Cut045042
  Tool = -> Part__Mirroring007
FEATURE [Part::Cut] Cut045044
  Base = -> Cut045043
  Tool = -> Part__Mirroring008
FEATURE [Part::MultiFuse] Fusion147
  Shapes = -> [Cut045044,Box053,Box052]
FEATURE [Part::Chamfer] Chamfer004
  Base = -> Fusion147
  Edges = 1 edges r=25: [Edge43]
FEATURE [Part::Chamfer] Chamfer005
  Base = -> Chamfer004
  Edges = 1 edges r=25: [Edge225]
FEATURE [Part::Chamfer] Chamfer006
  Base = -> Chamfer005
  Edges = 1 edges r=30: [Edge58]
FEATURE [Part::Chamfer] Chamfer007
  Base = -> Chamfer006
  Edges = 1 edges r=30: [Edge148]
FEATURE [Part::Fillet] Fillet
  Base = -> Chamfer007
  Edges = 1 edges r=2: [Edge233]
FEATURE [Part::Fillet] Fillet001
  Base = -> Fillet
  Edges = 1 edges r=2: [Edge6]
FEATURE [Part::Fillet] Fillet002
  Base = -> Fillet001
  Edges = 1 edges r=2: [Edge2]
FEATURE [Part::Fillet] Fillet003
  Base = -> Fillet002
  Edges = 1 edges r=2: [Edge357]
FEATURE [Part::Fillet] Fillet004
  Base = -> Fillet003
  Edges = 1 edges r=2: [Edge6]
FEATURE [Part::Fillet] Fillet005
  Base = -> Fillet004
  Edges = 1 edges r=2: [Edge2]
FEATURE [Part::Fillet] Fillet006
  Base = -> Fillet005
  Edges = 1 edges r=2: [Edge407]
FEATURE [Part::Fillet] Fillet007
  Base = -> Fillet006
  Edges = 1 edges r=2: [Edge2]
FEATURE [Part::Fillet] Fillet008
  Base = -> Fillet007
  Edges = 1 edges r=2: [Edge369]
FEATURE [Part::Fillet] Fillet009
  Base = -> Fillet008
  Edges = 1 edges r=2: [Edge2]
FEATURE [Part::Cylinder] Cylinder111  label="Cylinder207"
  Angle = 360
  Height = 28
  Placement = pos=(45,6,47) rot=(0.707107,0,0.707107;4.01426rad)
  Radius = 0.5
FEATURE [Part::Cylinder] Cylinder112  label="Cylinder208"
  Angle = 360
  Height = 28
  Placement = pos=(66,6,26) rot=(0.707107,0,0.707107;4.01426rad)
  Radius = 0.5
FEATURE [Part::Cut] Cut045045
  Base = -> Fillet009
  Tool = -> Cylinder111
FEATURE [Part::Cut] Cut045046
  Base = -> Cut045045
  Tool = -> Cylinder112
FEATURE [Part::Cylinder] Cylinder113  label="Cylinder209"
  Angle = 360
  Height = 28
  Placement = pos=(66,6,26) rot=(0.707107,0,0.707107;4.01426rad)
  Radius = 0.5
FEATURE [Part::Mirroring] Part__Mirroring010  label="Cylinder137 (Mirror #7)"
  Base = (0,0,0)
  Normal = (1,0,0)
  Placement = pos=(27,0,0) rot=(0,0,1;0rad)
  Source = -> Cylinder113
FEATURE [Part::Cylinder] Cylinder114  label="Cylinder210"
  Angle = 360
  Height = 28
  Placement = pos=(45,6,47) rot=(0.707107,0,0.707107;4.01426rad)
  Radius = 0.5
FEATURE [Part::Mirroring] Part__Mirroring011  label="Cylinder138 (Mirror #8)"
  Base = (0,0,0)
  Normal = (1,0,0)
  Placement = pos=(27,0,0) rot=(0,0,1;0rad)
  Source = -> Cylinder114
FEATURE [Part::Cut] Cut045047
  Base = -> Cut045046
  Tool = -> Part__Mirroring010
FEATURE [Part::Cut] Cut045048
  Base = -> Cut045047
  Tool = -> Part__Mirroring011
FEATURE [Part::Cylinder] Cylinder115  label="Arduino Cylinder191"
  Angle = 360
  Height = 28
  Placement = pos=(4,11,-8.6) rot=(1,0,0;1.5708rad)
  Radius = 1.6
FEATURE [Part::Cylinder] Cylinder116  label="Arduino Cylinder192"
  Angle = 360
  Height = 28
  Placement = pos=(31.9,11,-8.6) rot=(1,0,0;1.5708rad)
  Radius = 1.6
FEATURE [Part::Cylinder] Cylinder117  label="Arduino Cylinder193"
  Angle = 360
  Height = 28
  Placement = pos=(-11.2,11,-59.4) rot=(1,0,0;1.5708rad)
  Radius = 1.6
FEATURE [Part::Cylinder] Cylinder118  label="Arduino Cylinder194"
  Angle = 360
  Height = 28
  Placement = pos=(37,11,-60.7) rot=(1,0,0;1.5708rad)
  Radius = 1.6
FEATURE [Part::Cylinder] Cylinder119  label="Arduino Cylinder195"
  Angle = 360
  Height = 2.5
  Placement = pos=(4,13,-8.6) rot=(1,0,0;1.5708rad)
  Radius = 4
FEATURE [Part::Feature] Box014001
  Placement = pos=(3.88157,4,-2.89487) rot=(0,1,0;1.0472rad)
  shape: bbox 13.66 x 10 x 13.66 mm, 6 faces (baked)
FEATURE [Part::Feature] Box014002
  Placement = pos=(8.88157,4,-5.64487) rot=(0,1,0;2.0944rad)
  shape: bbox 13.66 x 10 x 13.66 mm, 6 faces (baked)
FEATURE [Part::Feature] Box014003
  Placement = pos=(9,4,-11.35) rot=(0,1,0;3.14159rad)
  shape: bbox 10 x 10 x 10 mm, 6 faces (baked)
FEATURE [Part::Feature] Box014004
  Placement = pos=(4.11843,4,-14.3051) rot=(0,1,0;4.18879rad)
  shape: bbox 13.66 x 10 x 13.66 mm, 6 faces (baked)
FEATURE [Part::Feature] Box014005
  Placement = pos=(-0.88157,4,-11.5551) rot=(0,-1,0;1.0472rad)
  shape: bbox 13.66 x 10 x 13.66 mm, 6 faces (baked)
FEATURE [Part::MultiFuse] Fusion148
  Shapes = -> [Box014001,Box014002,Box014004,Box014003,Box014005,Box014]
FEATURE [Part::Cut] Cut045049  label="M3 Nut004"
  Base = -> Cylinder119
  Placement = pos=(0,-3,0) rot=(0,0,1;0rad)
  Tool = -> Fusion148
FEATURE [Part::Box] Box014006  label="Not used Cube001"
  Height = 10
  Length = 10
  Placement = pos=(-1,4,-5.85) rot=(0,0,1;0rad)
  Width = 10
FEATURE [Part::Cylinder] Cylinder120  label="Arduino Cylinder196"
  Angle = 360
  Height = 2.5
  Placement = pos=(4,13,-8.6) rot=(1,0,0;1.5708rad)
  Radius = 4
FEATURE [Part::Feature] Box014007
  Placement = pos=(3.88157,4,-2.89487) rot=(0,1,0;1.0472rad)
  shape: bbox 13.66 x 10 x 13.66 mm, 6 faces (baked)
FEATURE [Part::Feature] Box014008
  Placement = pos=(8.88157,4,-5.64487) rot=(0,1,0;2.0944rad)
  shape: bbox 13.66 x 10 x 13.66 mm, 6 faces (baked)
FEATURE [Part::Feature] Box014009
  Placement = pos=(9,4,-11.35) rot=(0,1,0;3.14159rad)
  shape: bbox 10 x 10 x 10 mm, 6 faces (baked)
FEATURE [Part::Feature] Box014010
  Placement = pos=(4.11843,4,-14.3051) rot=(0,1,0;4.18879rad)
  shape: bbox 13.66 x 10 x 13.66 mm, 6 faces (baked)
FEATURE [Part::Feature] Box014011
  Placement = pos=(-0.88157,4,-11.5551) rot=(0,-1,0;1.0472rad)
  shape: bbox 13.66 x 10 x 13.66 mm, 6 faces (baked)
FEATURE [Part::MultiFuse] Fusion149
  Shapes = -> [Box014007,Box014008,Box014010,Box014009,Box014011,Box014006]
FEATURE [Part::Cut] Cut045050  label="M3 Nut005"
  Base = -> Cylinder120
  Placement = pos=(27.9,-3,0) rot=(0,0,1;0rad)
  Tool = -> Fusion149
FEATURE [Part::Box] Box014012  label="Not used Cube002"
  Height = 10
  Length = 10
  Placement = pos=(-1,4,-5.85) rot=(0,0,1;0rad)
  Width = 10
FEATURE [Part::Cylinder] Cylinder121  label="Arduino Cylinder197"
  Angle = 360
  Height = 2.5
  Placement = pos=(4,13,-8.6) rot=(1,0,0;1.5708rad)
  Radius = 4
FEATURE [Part::Feature] Box014013
  Placement = pos=(3.88157,4,-2.89487) rot=(0,1,0;1.0472rad)
  shape: bbox 13.66 x 10 x 13.66 mm, 6 faces (baked)
FEATURE [Part::Feature] Box014014
  Placement = pos=(8.88157,4,-5.64487) rot=(0,1,0;2.0944rad)
  shape: bbox 13.66 x 10 x 13.66 mm, 6 faces (baked)
FEATURE [Part::Feature] Box014015
  Placement = pos=(9,4,-11.35) rot=(0,1,0;3.14159rad)
  shape: bbox 10 x 10 x 10 mm, 6 faces (baked)
FEATURE [Part::Feature] Box014016
  Placement = pos=(4.11843,4,-14.3051) rot=(0,1,0;4.18879rad)
  shape: bbox 13.66 x 10 x 13.66 mm, 6 faces (baked)
FEATURE [Part::Feature] Box014017
  Placement = pos=(-0.88157,4,-11.5551) rot=(0,-1,0;1.0472rad)
  shape: bbox 13.66 x 10 x 13.66 mm, 6 faces (baked)
FEATURE [Part::MultiFuse] Fusion150
  Shapes = -> [Box014013,Box014014,Box014016,Box014015,Box014017,Box014012]
FEATURE [Part::Cut] Cut045051  label="M3 Nut006"
  Base = -> Cylinder121
  Placement = pos=(-15.2,-3,-50.8) rot=(0,0,1;0rad)
  Tool = -> Fusion150
FEATURE [Part::Box] Box014018  label="Not used Cube003"
  Height = 10
  Length = 10
  Placement = pos=(-1,4,-5.85) rot=(0,0,1;0rad)
  Width = 10
FEATURE [Part::Cylinder] Cylinder122  label="Arduino Cylinder198"
  Angle = 360
  Height = 2.5
  Placement = pos=(4,13,-8.6) rot=(1,0,0;1.5708rad)
  Radius = 4
FEATURE [Part::Feature] Box014019
  Placement = pos=(3.88157,4,-2.89487) rot=(0,1,0;1.0472rad)
  shape: bbox 13.66 x 10 x 13.66 mm, 6 faces (baked)
FEATURE [Part::Feature] Box014020
  Placement = pos=(8.88157,4,-5.64487) rot=(0,1,0;2.0944rad)
  shape: bbox 13.66 x 10 x 13.66 mm, 6 faces (baked)
FEATURE [Part::Feature] Box014021
  Placement = pos=(9,4,-11.35) rot=(0,1,0;3.14159rad)
  shape: bbox 10 x 10 x 10 mm, 6 faces (baked)
FEATURE [Part::Feature] Box014022
  Placement = pos=(4.11843,4,-14.3051) rot=(0,1,0;4.18879rad)
  shape: bbox 13.66 x 10 x 13.66 mm, 6 faces (baked)
FEATURE [Part::Feature] Box014023
  Placement = pos=(-0.88157,4,-11.5551) rot=(0,-1,0;1.0472rad)
  shape: bbox 13.66 x 10 x 13.66 mm, 6 faces (baked)
FEATURE [Part::MultiFuse] Fusion151
  Shapes = -> [Box014019,Box014020,Box014022,Box014021,Box014023,Box014018]
FEATURE [Part::Cut] Cut045052  label="M3 Nut007"
  Base = -> Cylinder122
  Placement = pos=(33,-3,-52.1) rot=(0,0,1;0rad)
  Tool = -> Fusion151
FEATURE [Part::Box] Box014024  label="Cube062"
  Height = 67
  Length = 65
  Placement = pos=(-16,-13,-6) rot=(0,0,1;0rad)
  Width = 8
FEATURE [Part::Cut] Cut045053  label="BAtt Holder"
  Base = -> Fusion110
  Tool = -> Box014024
FEATURE [Part::Cylinder] Cylinder123  label="Cylinder211"
  Angle = 360
  Height = 28
  Placement = pos=(45,6,47) rot=(0.707107,0,0.707107;4.01426rad)
  Radius = 0.5
FEATURE [Part::Cylinder] Cylinder124  label="Cylinder212"
  Angle = 360
  Height = 28
  Placement = pos=(66,6,26) rot=(0.707107,0,0.707107;4.01426rad)
  Radius = 0.5
FEATURE [Part::Cylinder] Cylinder125  label="Cylinder213"
  Angle = 360
  Height = 28
  Placement = pos=(45,6,47) rot=(0.707107,0,0.707107;4.01426rad)
  Radius = 0.5
FEATURE [Part::Cylinder] Cylinder126  label="Cylinder214"
  Angle = 360
  Height = 28
  Placement = pos=(66,6,26) rot=(0.707107,0,0.707107;4.01426rad)
  Radius = 0.5
FEATURE [Part::Mirroring] Part__Mirroring012  label="Cylinder211 (Mirror #13)"
  Base = (0,0,0)
  Normal = (1,0,0)
  Placement = pos=(27,0,0) rot=(0,0,1;0rad)
  Source = -> Cylinder125
FEATURE [Part::Mirroring] Part__Mirroring013  label="Cylinder212 (Mirror #14)"
  Base = (0,0,0)
  Normal = (1,0,0)
  Placement = pos=(27,0,0) rot=(0,0,1;0rad)
  Source = -> Cylinder126
FEATURE [Part::Chamfer] Chamfer008
  Base = -> Fusion104
  Edges = 1 edges r=0.5: [Edge67]
FEATURE [Part::Chamfer] Chamfer009
  Base = -> Chamfer008
  Edges = 1 edges r=0.5: [Edge6]
